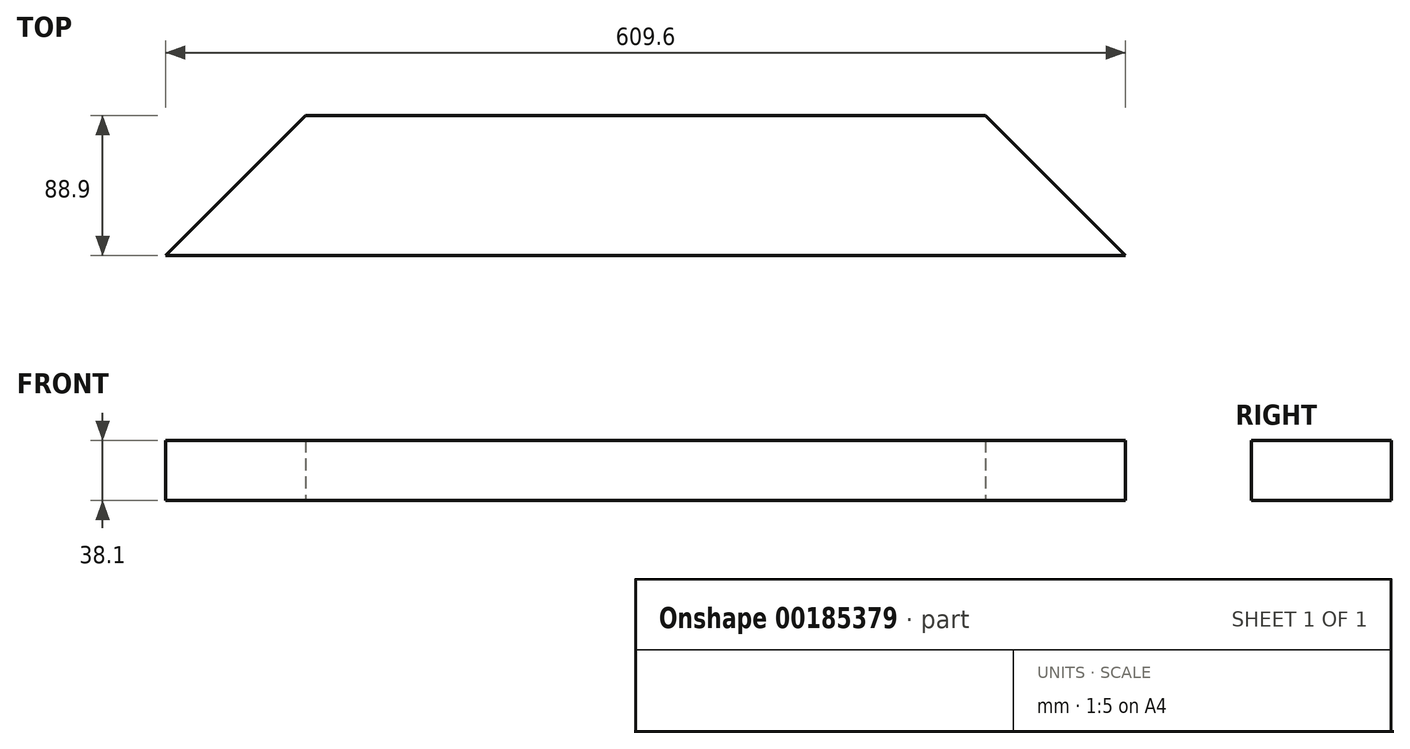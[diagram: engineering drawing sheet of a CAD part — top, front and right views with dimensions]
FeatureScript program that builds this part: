
annotation { "Feature Type Name" : "Feature", "Feature Type Description" : "" }
export const myFeature = defineFeature(function(context is Context, id is Id, definition is map)
    precondition{}
    {
        {
            var Q0;
            Q0=qCreatedBy(makeId("Top.planeOp"),FACE);
            var sketch = newSketch(context, id + "F0", { "sketchPlane" : qUnion([Q0])});
            skLineSegment(sketch, "E0", {"start": v(0, 0) * mm, "end": v(609.6, 0) * mm});
            skLineSegment(sketch, "E1", {"start": v(88.9, 88.9) * mm, "end": v(520.7, 88.9) * mm});
            skLineSegment(sketch, "E2", {"start": v(0, 0) * mm, "end": v(88.9, 88.9) * mm});
            skLineSegment(sketch, "E3", {"start": v(609.6, 0) * mm, "end": v(520.7, 88.9) * mm});
            skSolve(sketch);
        }
        {
            var Q0;
            Q0=makeQuery(id+"F0.imprint","IMPRINT",FACE,{"disambiguationData":[TD([[makeQuery(id+"F0.imprint","IMPRINT",EDGE,{"derivedFrom":sQuery(id+"F0.wireOp",EDGE,"E0")}),1.0]])]});
            extrude(context, id + "F1", {"entities" : qUnion([Q0]), "depth" : 38.1 * mm});
        }
    });
